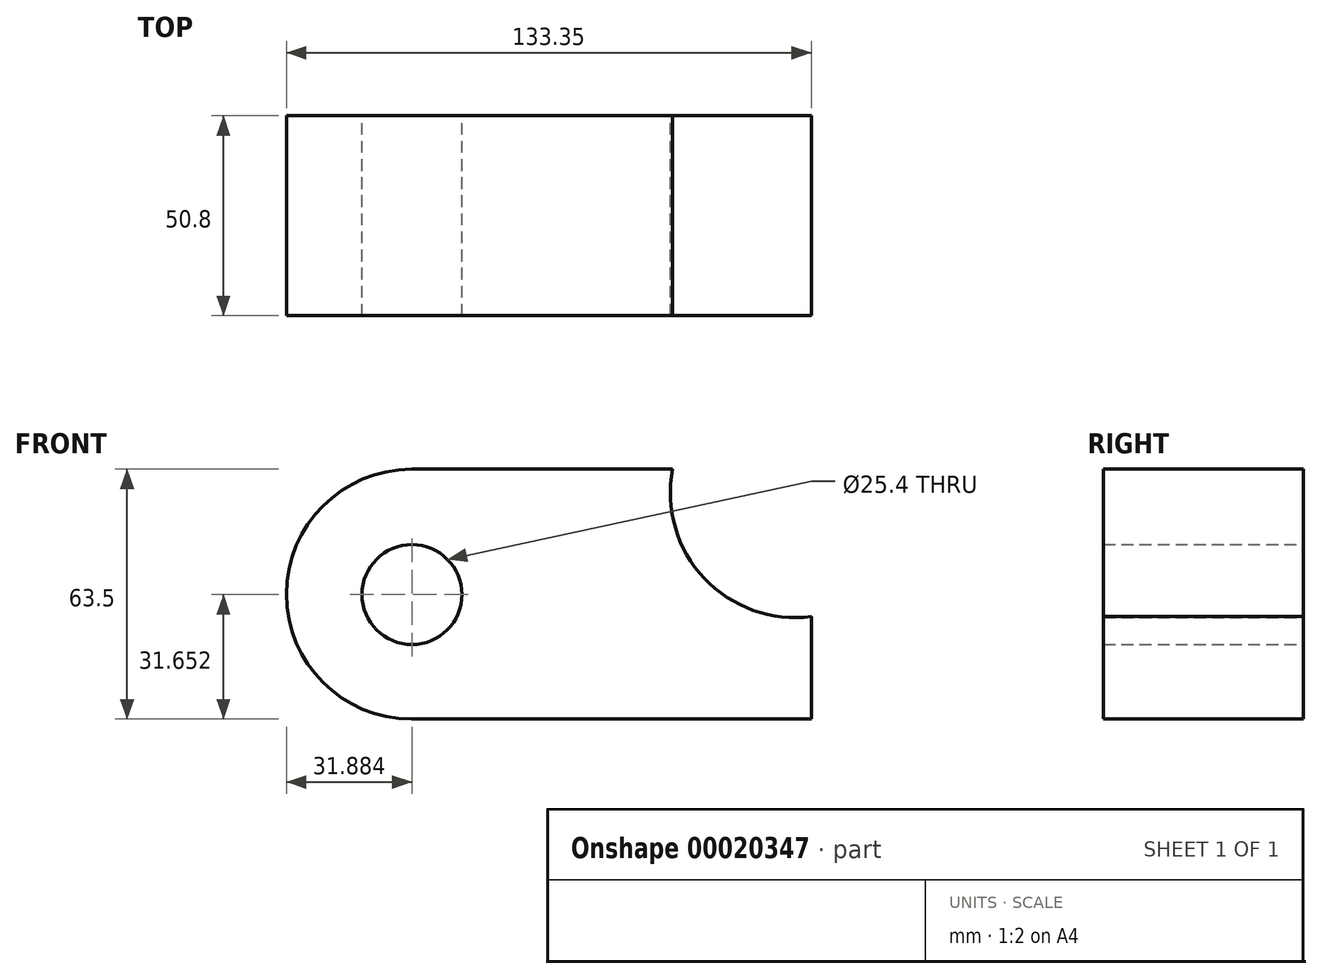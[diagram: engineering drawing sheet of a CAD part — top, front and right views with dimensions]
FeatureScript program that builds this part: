
annotation { "Feature Type Name" : "Feature", "Feature Type Description" : "" }
export const myFeature = defineFeature(function(context is Context, id is Id, definition is map)
    precondition{}
    {
        {
            var Q0;
            Q0=qCreatedBy(makeId("Front.planeOp"),FACE);
            var sketch = newSketch(context, id + "F0", { "sketchPlane" : qUnion([Q0])});
            skLineSegment(sketch, "E0", {"start": v(-67.03, 69.73) * mm, "end": v(-0.7, 69.73) * mm});
            skArc(sketch, "E1", {"start": v(-67.03, 69.73) * mm, "mid": v(-98.78, 37.98) * mm, "end": v(-67.03, 6.23) * mm});
            skLineSegment(sketch, "E2", {"start": v(-67.03, 6.23) * mm, "end": v(34.57, 6.23) * mm});
            skLineSegment(sketch, "E3", {"start": v(-67.03, 69.73) * mm, "end": v(-67.03, 37.98) * mm});
            skLineSegment(sketch, "E4", {"start": v(-67.03, 37.98) * mm, "end": v(-67.03, 0) * mm});
            skLineSegment(sketch, "E5", {"start": v(34.57, 32.3) * mm, "end": v(34.57, 6.23) * mm});
            skCircle(sketch, "E6", {"center": v(-66.9, 37.88) * mm, "radius": 12.7 * mm});
            skPoint(sketch, "E6.first.point", {"position": v(-67.03, 50.58) * mm});
            skPoint(sketch, "E6.second.point", {"position": v(-67.03, 25.18) * mm});
            skPoint(sketch, "E6.third.point", {"position": v(-54.2, 37.98) * mm});
            skArc(sketch, "E7", {"start": v(-0.7, 69.73) * mm, "mid": v(7.38, 42) * mm, "end": v(34.57, 32.3) * mm});
            skLineSegment(sketch, "E8", {"start": v(-67.03, 37.98) * mm, "end": v(-97.07, 48.27) * mm});
            skLineSegment(sketch, "E9", {"start": v(-76.11, 46.62) * mm, "end": v(-57.68, 29.14) * mm});
            skLineSegment(sketch, "E10", {"start": v(5.65, 44.01) * mm, "end": v(30.5, 63.78) * mm});
            skSolve(sketch);
        }
        {
            var Q0;
            Q0 = qSketchRegion(id + "F0", true);
            extrude(context, id + "F1", {"entities" : qUnion([Q0]), "depth" : 50.8 * mm});
        }
    });
